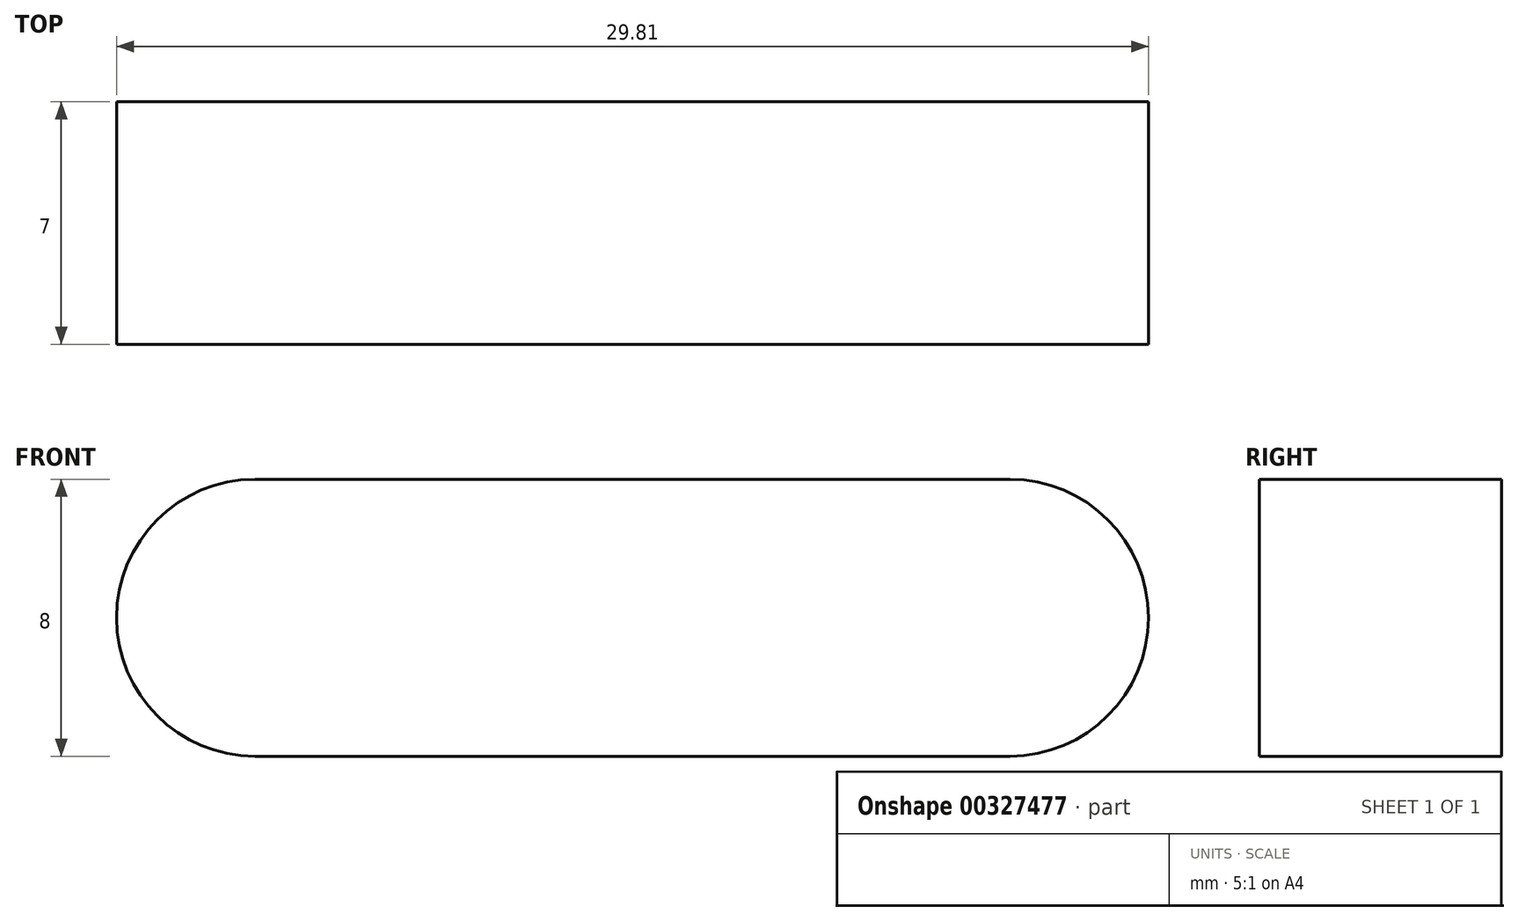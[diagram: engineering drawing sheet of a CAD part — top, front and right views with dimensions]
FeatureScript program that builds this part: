
annotation { "Feature Type Name" : "Feature", "Feature Type Description" : "" }
export const myFeature = defineFeature(function(context is Context, id is Id, definition is map)
    precondition{}
    {
        {
            var Q0;
            Q0=qCreatedBy(makeId("Front.planeOp"),FACE);
            var sketch = newSketch(context, id + "F0", { "sketchPlane" : qUnion([Q0])});
            skLineSegment(sketch, "E0", {"start": v(0, 0) * mm, "end": v(0, 8) * mm});
            skArc(sketch, "E1", {"start": v(0, 8) * mm, "mid": v(-4, 4) * mm, "end": v(0, 0) * mm});
            skLineSegment(sketch, "E2", {"start": v(0, 8) * mm, "end": v(21.8, 8) * mm});
            skLineSegment(sketch, "E3", {"start": v(0, 0) * mm, "end": v(21.8, 0) * mm});
            skLineSegment(sketch, "E4", {"start": v(21.8, 8) * mm, "end": v(21.8, 0) * mm});
            skArc(sketch, "E5", {"start": v(21.8, 0) * mm, "mid": v(25.8, 4) * mm, "end": v(21.8, 8) * mm});
            skSolve(sketch);
        }
        {
            var Q0;
            Q0 = qSketchRegion(id + "F0", true);
            extrude(context, id + "F1", {"entities" : qUnion([Q0]), "depth" : 7 * mm});
        }
    });
